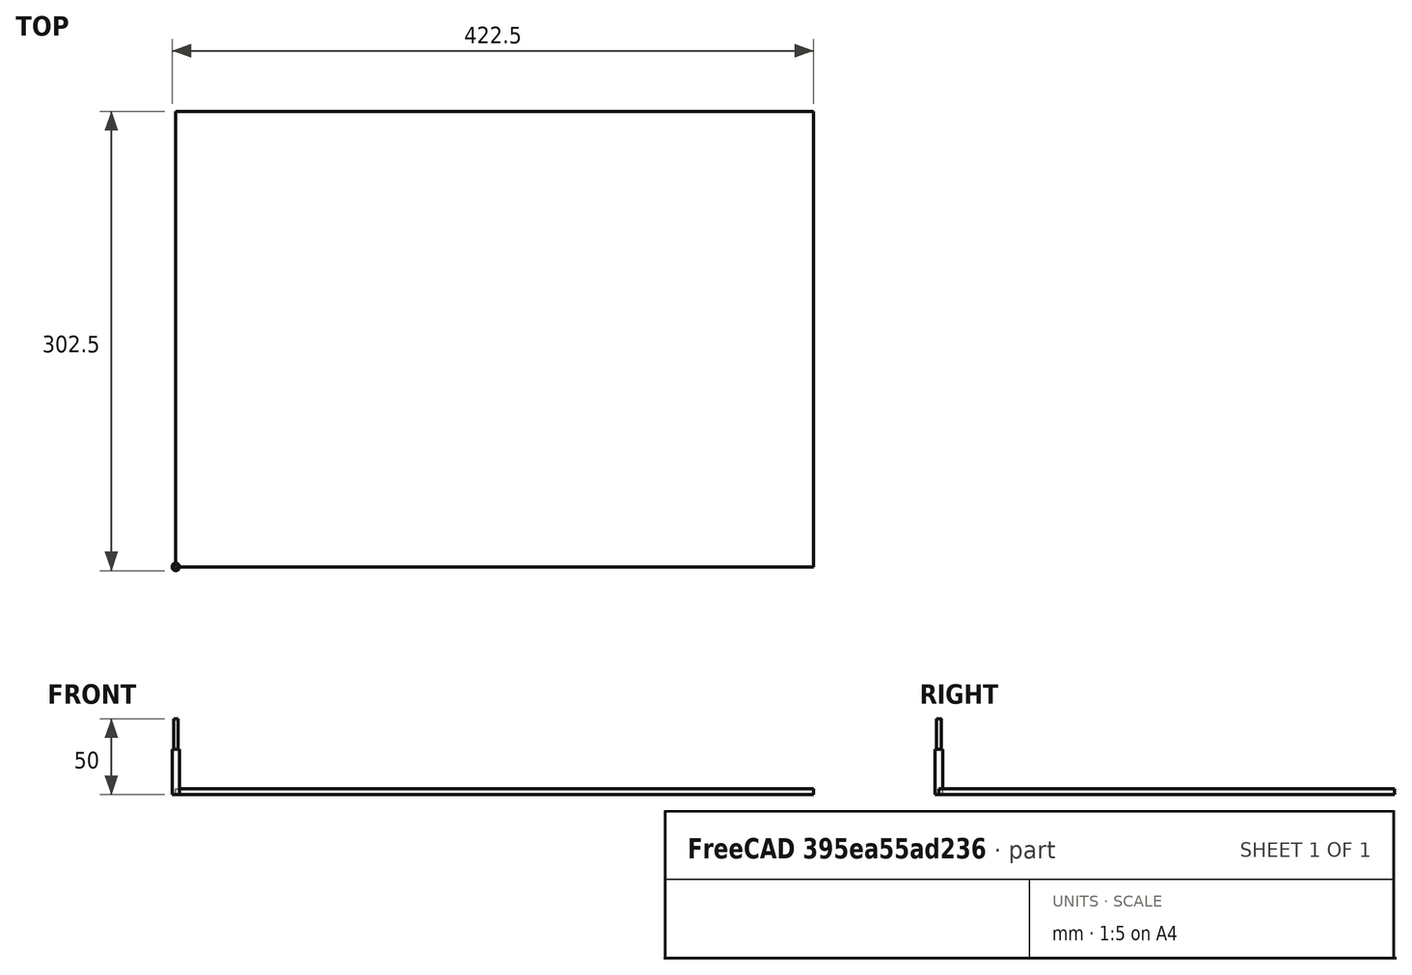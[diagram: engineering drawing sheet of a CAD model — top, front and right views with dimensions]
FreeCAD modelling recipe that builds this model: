
FCSTD DOCUMENT  (FreeCAD 1.0R39109 (Git))
Label: HousingAtari_T02
License: All rights reserved
LicenseURL: https://en.wikipedia.org/wiki/All_rights_reserved
objects: Sketcher::SketchObject×6, Part::Part2DObjectPython×5, Path::FeaturePython×3, App::DocumentObjectGroup×3, Part::FeaturePython×2, PartDesign::Body×1, App::FeaturePython×1, Mesh::FeaturePython×1
note: 20 computed .brp shape members not serialized (recipe doc carries the construction recipe); baked Part::Feature solids carry a one-line shape summary decoded from their .brp

FEATURE [Sketcher::SketchObject] Sketch  label="A3"
  ArcFitTolerance = 0
  FullyConstrained = false
  MakeInternals = false
  MapMode = 5
  sketch-geometry (7):
    g0: LineSegment StartX=0 StartY=420 StartZ=0 EndX=0 EndY=0 EndZ=0
    g1: LineSegment StartX=0 StartY=420 StartZ=0 EndX=148.5 EndY=420 EndZ=0
    g2: LineSegment StartX=148.5 StartY=420 StartZ=0 EndX=148.5 EndY=0 EndZ=0
    g3: LineSegment StartX=148.5 StartY=420 StartZ=0 EndX=297 EndY=420 EndZ=0
    g4: LineSegment StartX=297 StartY=420 StartZ=0 EndX=297 EndY=210 EndZ=0
    g5: LineSegment StartX=297 StartY=210 StartZ=0 EndX=297 EndY=0 EndZ=0
    g6: LineSegment StartX=297 StartY=210 StartZ=0 EndX=0 EndY=210 EndZ=0
  constraints (21):
    c: Vertical(g0)
    c: DistanceY(g0,g0) = 420
    c: Coincident(g1,g0)
    c: Horizontal(g1)
    c: Coincident(g2,g1)
    c: Coincident(g3,g1)
    c: Horizontal(g3)
    c: Equal(g1,g3)
    c: Vertical(g2)
    c: DistanceX(g0,g3) = 297
    c: Coincident(g4,g3)
    c: Vertical(g4)
    c: Coincident(g5,g4)
    c: PointOnObject(g5,g-1)
    c: Vertical(g5)
    c: Equal(g5,g4)
    c: PointOnObject(g0,g-1)
    c: PointOnObject(g0,g-2)
    c: Coincident(g6,g4)
    c: PointOnObject(g6,g0)
    c: Horizontal(g6)
FEATURE [Sketcher::SketchObject] Sketch001  label="BOX-OUTLINE"
  ArcFitTolerance = 0
  ExternalGeometry = -> [Sketch]
  FullyConstrained = false
  MakeInternals = false
  MapMode = 5
  sketch-geometry (60):
    g0: LineSegment StartX=83.5 StartY=362.836 StartZ=0 EndX=83.5 EndY=292.836 EndZ=0
    g1: LineSegment StartX=83.5 StartY=292.836 StartZ=0 EndX=83.5 EndY=222.836 EndZ=0
    g2: LineSegment StartX=83.5 StartY=222.836 StartZ=0 EndX=148.5 EndY=222.836 EndZ=0
    g3: LineSegment StartX=148.5 StartY=222.836 StartZ=0 EndX=213.5 EndY=222.836 EndZ=0
    g4: LineSegment StartX=213.5 StartY=222.836 StartZ=0 EndX=213.5 EndY=292.836 EndZ=0
    g5: LineSegment StartX=213.5 StartY=292.836 StartZ=0 EndX=213.5 EndY=362.836 EndZ=0
    g6: LineSegment StartX=213.5 StartY=362.836 StartZ=0 EndX=148.5 EndY=362.836 EndZ=0
    g7: LineSegment StartX=148.5 StartY=362.836 StartZ=0 EndX=83.5 EndY=362.836 EndZ=0
    g8: LineSegment StartX=83.5 StartY=222.836 StartZ=0 EndX=83.5 EndY=218.836 EndZ=0
    g9: LineSegment StartX=83.5 StartY=218.836 StartZ=0 EndX=213.5 EndY=218.836 EndZ=0
    g10: LineSegment StartX=213.5 StartY=218.836 StartZ=0 EndX=213.5 EndY=222.836 EndZ=0
    g11: LineSegment StartX=213.5 StartY=222.836 StartZ=0 EndX=217.5 EndY=222.836 EndZ=0
    g12: LineSegment StartX=217.5 StartY=222.836 StartZ=0 EndX=217.5 EndY=362.836 EndZ=0
    g13: LineSegment StartX=217.5 StartY=362.836 StartZ=0 EndX=213.5 EndY=362.836 EndZ=0
    g14: LineSegment StartX=213.5 StartY=362.836 StartZ=0 EndX=213.5 EndY=366.836 EndZ=0
    g15: LineSegment StartX=213.5 StartY=366.836 StartZ=0 EndX=83.5 EndY=366.836 EndZ=0
    g16: LineSegment StartX=83.5 StartY=366.836 StartZ=0 EndX=83.5 EndY=362.836 EndZ=0
    g17: LineSegment StartX=83.5 StartY=222.836 StartZ=0 EndX=79.5 EndY=222.836 EndZ=0
    g18: LineSegment StartX=79.5 StartY=222.836 StartZ=0 EndX=79.5 EndY=362.836 EndZ=0
    g19: LineSegment StartX=79.5 StartY=362.836 StartZ=0 EndX=83.5 EndY=362.836 EndZ=0
    g20: LineSegment StartX=83.5 StartY=218.836 StartZ=0 EndX=83.5 EndY=188.836 EndZ=0
    g21: LineSegment StartX=83.5 StartY=188.836 StartZ=0 EndX=213.5 EndY=188.836 EndZ=0
    g22: LineSegment StartX=213.5 StartY=188.836 StartZ=0 EndX=213.5 EndY=218.836 EndZ=0
    g23: LineSegment StartX=217.5 StartY=222.836 StartZ=0 EndX=243.5 EndY=222.836 EndZ=0
    g24: LineSegment StartX=243.5 StartY=222.836 StartZ=0 EndX=243.5 EndY=362.836 EndZ=0
    g25: LineSegment StartX=243.5 StartY=362.836 StartZ=0 EndX=217.5 EndY=362.836 EndZ=0
    g26: LineSegment StartX=213.5 StartY=366.836 StartZ=0 EndX=213.5 EndY=396.836 EndZ=0
    g27: LineSegment StartX=213.5 StartY=396.836 StartZ=0 EndX=83.5 EndY=396.836 EndZ=0
    g28: LineSegment StartX=83.5 StartY=396.836 StartZ=0 EndX=83.5 EndY=366.836 EndZ=0
    g29: LineSegment StartX=79.5 StartY=362.836 StartZ=0 EndX=53.5 EndY=362.836 EndZ=0
    g30: LineSegment StartX=53.5 StartY=362.836 StartZ=0 EndX=53.5 EndY=222.836 EndZ=0
    g31: LineSegment StartX=53.5 StartY=222.836 StartZ=0 EndX=79.5 EndY=222.836 EndZ=0
    g32: LineSegment StartX=213.5 StartY=188.836 StartZ=0 EndX=217.5 EndY=188.836 EndZ=0
    g33: LineSegment StartX=217.5 StartY=188.836 StartZ=0 EndX=217.5 EndY=222.836 EndZ=0
    g34: LineSegment StartX=213.5 StartY=218.836 StartZ=0 EndX=243.5 EndY=218.836 EndZ=0
    g35: LineSegment StartX=243.5 StartY=218.836 StartZ=0 EndX=243.5 EndY=222.836 EndZ=0
    g36: LineSegment StartX=213.5 StartY=366.836 StartZ=0 EndX=243.5 EndY=366.836 EndZ=0
    g37: LineSegment StartX=243.5 StartY=366.836 StartZ=0 EndX=243.5 EndY=362.836 EndZ=0
    g38: LineSegment StartX=217.5 StartY=362.836 StartZ=0 EndX=217.5 EndY=396.836 EndZ=0
    g39: LineSegment StartX=217.5 StartY=396.836 StartZ=0 EndX=213.5 EndY=396.836 EndZ=0
    g40: LineSegment StartX=83.5 StartY=396.836 StartZ=0 EndX=79.5 EndY=396.836 EndZ=0
    g41: LineSegment StartX=79.5 StartY=396.836 StartZ=0 EndX=79.5 EndY=362.836 EndZ=0
    g42: LineSegment StartX=53.5 StartY=362.836 StartZ=0 EndX=53.5 EndY=366.836 EndZ=0
    g43: LineSegment StartX=53.5 StartY=366.836 StartZ=0 EndX=83.5 EndY=366.836 EndZ=0
    g44: LineSegment StartX=53.5 StartY=222.836 StartZ=0 EndX=53.5 EndY=218.836 EndZ=0
    g45: LineSegment StartX=53.5 StartY=218.836 StartZ=0 EndX=83.5 EndY=218.836 EndZ=0
    g46: LineSegment StartX=79.5 StartY=222.836 StartZ=0 EndX=79.5 EndY=188.836 EndZ=0
    g47: LineSegment StartX=79.5 StartY=188.836 StartZ=0 EndX=83.5 EndY=188.836 EndZ=0
    g48: LineSegment StartX=83.5 StartY=188.836 StartZ=0 EndX=83.5 EndY=44.8363 EndZ=0
    g49: LineSegment StartX=83.5 StartY=44.8363 StartZ=0 EndX=213.5 EndY=44.8363 EndZ=0
    g50: LineSegment StartX=213.5 StartY=44.8363 StartZ=0 EndX=213.5 EndY=188.836 EndZ=0
    g51: LineSegment StartX=79.5 StartY=188.836 StartZ=0 EndX=79.5 EndY=48.8363 EndZ=0
    g52: LineSegment StartX=79.5 StartY=48.8363 StartZ=0 EndX=217.5 EndY=48.8363 EndZ=0
    g53: LineSegment StartX=217.5 StartY=48.8363 StartZ=0 EndX=217.5 EndY=188.836 EndZ=0
    g54: LineSegment StartX=79.5 StartY=192.836 StartZ=0 EndX=217.5 EndY=192.836 EndZ=0
    g55: LineSegment StartX=79.5 StartY=48.8363 StartZ=0 EndX=79.5 EndY=44.8363 EndZ=0
    g56: LineSegment StartX=217.5 StartY=48.8363 StartZ=0 EndX=217.5 EndY=44.8363 EndZ=0
    g57: LineSegment StartX=79.5 StartY=392.836 StartZ=0 EndX=217.5 EndY=392.836 EndZ=0
    g58: LineSegment StartX=247.5 StartY=366.836 StartZ=0 EndX=247.5 EndY=218.836 EndZ=0
    g59: LineSegment StartX=49.5 StartY=366.836 StartZ=0 EndX=49.5 EndY=218.836 EndZ=0
  constraints (166):
    c: Vertical(g0)
    c: Coincident(g1,g0)
    c: Vertical(g1)
    c: Coincident(g2,g1)
    c: Horizontal(g2)
    c: Coincident(g3,g2)
    c: Horizontal(g3)
    c: Coincident(g4,g3)
    c: Vertical(g4)
    c: Coincident(g5,g4)
    c: Vertical(g5)
    c: Horizontal(g6)
    c: Coincident(g7,g6)
    c: Coincident(g7,g0)
    c: Horizontal(g7)
    c: Vertical(g2,g6)
    c: Horizontal(g0,g4)
    c: Equal(g4,g5)
    c: Equal(g7,g6)
    c: Coincident(g5,g6)
    c: DistanceY(g1,g0) = 140
    c: DistanceX(g0,g5) = 130
    c: Coincident(g8,g1)
    c: Vertical(g8)
    c: Coincident(g9,g8)
    c: Horizontal(g9)
    c: Coincident(g10,g9)
    c: Coincident(g10,g3)
    c: Vertical(g10)
    c: Coincident(g11,g3)
    c: Horizontal(g11)
    c: Coincident(g12,g11)
    c: Vertical(g12)
    c: Coincident(g13,g12)
    c: Coincident(g13,g5)
    c: Horizontal(g13)
    c: Equal(g10,g11)
    c: DistanceY(g10,g10) = 4
    c: Coincident(g14,g5)
    c: Vertical(g14)
    c: Coincident(g15,g14)
    c: Horizontal(g15)
    c: Coincident(g16,g15)
    c: Coincident(g16,g0)
    c: Vertical(g16)
    c: Equal(g13,g14)
    c: Coincident(g17,g1)
    c: Horizontal(g17)
    c: Coincident(g18,g17)
    c: Vertical(g18)
    c: Coincident(g19,g18)
    c: Coincident(g19,g0)
    c: Horizontal(g19)
    c: Equal(g16,g19)
    c: Coincident(g20,g8)
    c: Vertical(g20)
    c: Coincident(g21,g20)
    c: Horizontal(g21)
    c: Coincident(g22,g21)
    c: Coincident(g22,g9)
    c: Coincident(g23,g11)
    c: Horizontal(g23)
    c: Coincident(g24,g23)
    c: Vertical(g24)
    c: Coincident(g25,g24)
    c: Coincident(g25,g12)
    c: Horizontal(g25)
    c: Coincident(g26,g14)
    c: Vertical(g26)
    c: Coincident(g27,g26)
    c: Horizontal(g27)
    c: Coincident(g28,g27)
    c: Coincident(g28,g15)
    c: Coincident(g29,g18)
    c: Horizontal(g29)
    c: Coincident(g30,g29)
    c: Vertical(g30)
    c: Coincident(g31,g30)
    c: Coincident(g31,g17)
    c: Horizontal(g31)
    c: Vertical(g22)
    c: Coincident(g32,g21)
    c: Horizontal(g32)
    c: Coincident(g33,g32)
    c: Coincident(g33,g11)
    c: Vertical(g33)
    c: Coincident(g34,g9)
    c: Horizontal(g34)
    c: Coincident(g35,g34)
    c: Coincident(g35,g23)
    c: Coincident(g36,g14)
    c: Horizontal(g36)
    c: Coincident(g37,g36)
    c: Coincident(g37,g24)
    c: Coincident(g38,g12)
    c: Vertical(g38)
    c: Coincident(g39,g38)
    c: Coincident(g39,g26)
    c: Horizontal(g39)
    c: Coincident(g40,g27)
    c: Horizontal(g40)
    c: Coincident(g41,g40)
    c: Coincident(g41,g18)
    c: Coincident(g42,g29)
    c: Vertical(g42)
    c: Coincident(g43,g42)
    c: Coincident(g43,g15)
    c: Coincident(g44,g30)
    c: Vertical(g44)
    c: Coincident(g45,g44)
    c: Coincident(g45,g8)
    c: Horizontal(g45)
    c: Coincident(g46,g17)
    c: Coincident(g47,g46)
    c: Coincident(g47,g20)
    c: Vertical(g37)
    c: Vertical(g46)
    c: Vertical(g35)
    c: Horizontal(g43)
    c: Horizontal(g47)
    c: DistanceY(g15,g27) = 30
    c: Vertical(g41)
    c: Vertical(g28)
    c: DistanceY(g22,g22) = 30
    c: Distance(g43,g43) = 30
    c: DistanceX(g34,g34) = 30
    c: Coincident(g48,g20)
    c: Vertical(g48)
    c: Coincident(g49,g48)
    c: Horizontal(g49)
    c: Coincident(g50,g49)
    c: Coincident(g50,g21)
    c: Vertical(g50)
    c: Coincident(g51,g46)
    c: Vertical(g51)
    c: Coincident(g52,g51)
    c: Horizontal(g52)
    c: Coincident(g53,g52)
    c: Coincident(g53,g32)
    c: Vertical(g53)
    c: PointOnObject(g54,g46)
    c: PointOnObject(g54,g33)
    c: Horizontal(g54)
    c: DistanceY(g46,g54) = 4
    c: Coincident(g55,g51)
    c: PointOnObject(g55,g49)
    c: Vertical(g55)
    c: DistanceY(g55,g55) = 4
    c: DistanceY(g51,g51) = 140
    c: DistanceY(g34,g36) = 148
    c: Coincident(g56,g52)
    c: PointOnObject(g56,g49)
    c: Vertical(g56)
    c: DistanceY(g56,g54) = 148
    c: PointOnObject(g57,g41)
    c: PointOnObject(g57,g38)
    c: Horizontal(g57)
    c: DistanceY(g57,g38) = 4
    c: PointOnObject(g6,g-3)
    c: PointOnObject(g58,g36)
    c: PointOnObject(g58,g34)
    c: Vertical(g58)
    c: PointOnObject(g59,g43)
    c: PointOnObject(g59,g45)
    c: Vertical(g59)
    c: DistanceX(g42,g59) = -4
FEATURE [PartDesign::Body] Body
  AllowCompound = false
  Group = -> [Sketch,Sketch001]
  Origin = -> Origin
FEATURE [Sketcher::SketchObject] Sketch002  label="CUT-BOX-BASE"
  ArcFitTolerance = 0
  ExternalGeometry = -> [Sketch001,Sketch]
  FullyConstrained = true
  MakeInternals = false
  MapMode = 5
  sketch-geometry (44):
    g0: LineSegment StartX=107.1 StartY=366.836 StartZ=0 EndX=79.5 EndY=366.836 EndZ=0
    g1: LineSegment StartX=189.9 StartY=366.836 StartZ=0 EndX=217.5 EndY=366.836 EndZ=0
    g2: LineSegment StartX=134.7 StartY=366.836 StartZ=0 EndX=162.3 EndY=366.836 EndZ=0
    g3: LineSegment StartX=162.3 StartY=362.836 StartZ=0 EndX=189.9 EndY=362.836 EndZ=0
    g4: LineSegment StartX=107.1 StartY=362.836 StartZ=0 EndX=134.7 EndY=362.836 EndZ=0
    g5: LineSegment StartX=107.1 StartY=366.836 StartZ=0 EndX=107.1 EndY=362.836 EndZ=0
    g6: LineSegment StartX=134.7 StartY=366.836 StartZ=0 EndX=134.7 EndY=362.836 EndZ=0
    g7: LineSegment StartX=162.3 StartY=366.836 StartZ=0 EndX=162.3 EndY=362.836 EndZ=0
    g8: LineSegment StartX=189.9 StartY=362.836 StartZ=0 EndX=189.9 EndY=366.836 EndZ=0
    g9: LineSegment [constr] StartX=107.1 StartY=362.836 StartZ=0 EndX=107.1 EndY=222.836 EndZ=0
    g10: LineSegment [constr] StartX=134.7 StartY=362.836 StartZ=0 EndX=134.7 EndY=222.836 EndZ=0
    g11: LineSegment [constr] StartX=162.3 StartY=362.836 StartZ=0 EndX=162.3 EndY=222.836 EndZ=0
    g12: LineSegment [constr] StartX=189.9 StartY=362.836 StartZ=0 EndX=189.9 EndY=222.836 EndZ=0
    g13: LineSegment StartX=79.5 StartY=218.836 StartZ=0 EndX=107.1 EndY=218.836 EndZ=0
    g14: LineSegment StartX=107.1 StartY=218.836 StartZ=0 EndX=107.1 EndY=222.836 EndZ=0
    g15: LineSegment StartX=107.1 StartY=222.836 StartZ=0 EndX=134.7 EndY=222.836 EndZ=0
    g16: LineSegment StartX=134.7 StartY=222.836 StartZ=0 EndX=134.7 EndY=218.836 EndZ=0
    g17: LineSegment StartX=134.7 StartY=218.836 StartZ=0 EndX=162.3 EndY=218.836 EndZ=0
    g18: LineSegment StartX=162.3 StartY=218.836 StartZ=0 EndX=162.3 EndY=222.836 EndZ=0
    g19: LineSegment StartX=162.3 StartY=222.836 StartZ=0 EndX=189.9 EndY=222.836 EndZ=0
    g20: LineSegment StartX=189.9 StartY=222.836 StartZ=0 EndX=189.9 EndY=218.836 EndZ=0
    g21: LineSegment StartX=189.9 StartY=218.836 StartZ=0 EndX=217.5 EndY=218.836 EndZ=0
    g22: LineSegment StartX=79.5 StartY=366.836 StartZ=0 EndX=79.5 EndY=336.163 EndZ=0
    g23: LineSegment StartX=79.5 StartY=305.49 StartZ=0 EndX=79.5 EndY=274.818 EndZ=0
    g24: LineSegment StartX=79.5 StartY=218.836 StartZ=0 EndX=79.5 EndY=244.145 EndZ=0
    g25: LineSegment StartX=79.5 StartY=336.163 StartZ=0 EndX=83.5 EndY=336.163 EndZ=0
    g26: LineSegment StartX=79.5 StartY=305.49 StartZ=0 EndX=83.5 EndY=305.49 EndZ=0
    g27: LineSegment StartX=79.5 StartY=274.818 StartZ=0 EndX=83.5 EndY=274.818 EndZ=0
    g28: LineSegment StartX=79.5 StartY=244.145 StartZ=0 EndX=83.5 EndY=244.145 EndZ=0
    g29: LineSegment StartX=83.5 StartY=305.49 StartZ=0 EndX=83.5 EndY=336.163 EndZ=0
    g30: LineSegment StartX=83.5 StartY=244.145 StartZ=0 EndX=83.5 EndY=274.818 EndZ=0
    g31: LineSegment [constr] StartX=83.5 StartY=336.163 StartZ=0 EndX=213.5 EndY=336.163 EndZ=0
    g32: LineSegment [constr] StartX=83.5 StartY=305.49 StartZ=0 EndX=213.5 EndY=305.49 EndZ=0
    g33: LineSegment [constr] StartX=83.5 StartY=274.818 StartZ=0 EndX=213.5 EndY=274.818 EndZ=0
    g34: LineSegment [constr] StartX=83.5 StartY=244.145 StartZ=0 EndX=213.5 EndY=244.145 EndZ=0
    g35: LineSegment StartX=217.5 StartY=366.836 StartZ=0 EndX=217.5 EndY=336.163 EndZ=0
    g36: LineSegment StartX=213.5 StartY=336.163 StartZ=0 EndX=217.5 EndY=336.163 EndZ=0
    g37: LineSegment StartX=213.5 StartY=305.49 StartZ=0 EndX=213.5 EndY=336.163 EndZ=0
    g38: LineSegment StartX=213.5 StartY=305.49 StartZ=0 EndX=217.5 EndY=305.49 EndZ=0
    g39: LineSegment StartX=213.5 StartY=274.818 StartZ=0 EndX=213.5 EndY=244.145 EndZ=0
    g40: LineSegment StartX=213.5 StartY=244.145 StartZ=0 EndX=217.5 EndY=244.145 EndZ=0
    g41: LineSegment StartX=217.5 StartY=244.145 StartZ=0 EndX=217.5 EndY=218.836 EndZ=0
    g42: LineSegment StartX=213.5 StartY=274.818 StartZ=0 EndX=217.5 EndY=274.818 EndZ=0
    g43: LineSegment StartX=217.5 StartY=274.818 StartZ=0 EndX=217.5 EndY=305.49 EndZ=0
  constraints (126):
    c: PointOnObject(g0,g-5)
    c: PointOnObject(g0,g-9)
    c: Horizontal(g0)
    c: PointOnObject(g1,g-5)
    c: PointOnObject(g1,g-10)
    c: Horizontal(g1)
    c: PointOnObject(g2,g-5)
    c: PointOnObject(g2,g-5)
    c: PointOnObject(g3,g-4)
    c: PointOnObject(g3,g-4)
    c: PointOnObject(g4,g-3)
    c: PointOnObject(g4,g-3)
    c: Coincident(g5,g0)
    c: Coincident(g5,g4)
    c: Coincident(g6,g2)
    c: Coincident(g6,g4)
    c: Coincident(g7,g2)
    c: Coincident(g7,g3)
    c: Coincident(g8,g3)
    c: Coincident(g8,g1)
    c: Vertical(g5)
    c: Vertical(g6)
    c: Vertical(g7)
    c: Vertical(g8)
    c: Equal(g0,g1)
    c: Equal(g4,g2)
    c: Equal(g3,g2)
    c: Equal(g0,g2)
    c: Coincident(g9,g4)
    c: PointOnObject(g9,g-6)
    c: Vertical(g9)
    c: Coincident(g10,g4)
    c: PointOnObject(g10,g-6)
    c: Vertical(g10)
    c: Coincident(g11,g3)
    c: PointOnObject(g11,g-8)
    c: Vertical(g11)
    c: Coincident(g12,g3)
    c: PointOnObject(g12,g-8)
    c: Vertical(g12)
    c: PointOnObject(g13,g-12)
    c: PointOnObject(g13,g-7)
    c: Horizontal(g13)
    c: Coincident(g14,g13)
    c: Coincident(g14,g9)
    c: Coincident(g15,g9)
    c: Coincident(g15,g10)
    c: Coincident(g16,g10)
    c: PointOnObject(g16,g-7)
    c: Coincident(g17,g16)
    c: PointOnObject(g17,g-7)
    c: Coincident(g18,g17)
    c: Coincident(g18,g11)
    c: Coincident(g19,g11)
    c: Coincident(g19,g12)
    c: Coincident(g20,g12)
    c: PointOnObject(g20,g-7)
    c: Vertical(g20)
    c: Coincident(g21,g20)
    c: PointOnObject(g21,g-11)
    c: Horizontal(g21)
    c: Vertical(g14)
    c: Vertical(g16)
    c: Vertical(g18)
    c: DistanceY(g21,g1) = 148
    c: DistanceX(g0,g1) = 138
    c: Coincident(g22,g0)
    c: PointOnObject(g22,g-14)
    c: PointOnObject(g23,g-14)
    c: PointOnObject(g23,g-14)
    c: Coincident(g24,g13)
    c: PointOnObject(g24,g-14)
    c: Coincident(g25,g22)
    c: PointOnObject(g25,g-16)
    c: Horizontal(g25)
    c: Coincident(g26,g23)
    c: PointOnObject(g26,g-16)
    c: Horizontal(g26)
    c: Coincident(g27,g23)
    c: PointOnObject(g27,g-17)
    c: Coincident(g28,g24)
    c: PointOnObject(g28,g-17)
    c: Horizontal(g28)
    c: Horizontal(g27)
    c: Equal(g22,g23)
    c: Coincident(g29,g26)
    c: Coincident(g29,g25)
    c: Coincident(g30,g28)
    c: Coincident(g30,g27)
    c: Equal(g30,g23)
    c: Equal(g29,g30)
    c: Equal(g29,g22)
    c: Coincident(g31,g25)
    c: PointOnObject(g31,g-18)
    c: Horizontal(g31)
    c: Coincident(g32,g26)
    c: PointOnObject(g32,g-18)
    c: Horizontal(g32)
    c: Coincident(g33,g27)
    c: PointOnObject(g33,g-19)
    c: Horizontal(g33)
    c: Coincident(g34,g28)
    c: PointOnObject(g34,g-19)
    c: Horizontal(g34)
    c: Coincident(g35,g1)
    c: PointOnObject(g35,g-15)
    c: Coincident(g36,g31)
    c: Coincident(g36,g35)
    c: Coincident(g37,g32)
    c: Coincident(g37,g31)
    c: Coincident(g38,g32)
    c: PointOnObject(g38,g-15)
    c: Coincident(g39,g33)
    c: Coincident(g39,g34)
    c: Coincident(g40,g34)
    c: PointOnObject(g40,g-15)
    c: Coincident(g41,g40)
    c: Coincident(g41,g21)
    c: Horizontal(g36)
    c: Horizontal(g38)
    c: Horizontal(g40)
    c: Coincident(g42,g33)
    c: PointOnObject(g42,g-15)
    c: Horizontal(g42)
    c: Coincident(g43,g42)
    c: Coincident(g43,g38)
FEATURE [Sketcher::SketchObject] Sketch003  label="CUT-Functional"
  ArcFitTolerance = 0
  ExternalGeometry = -> [Sketch]
  FullyConstrained = false
  MakeInternals = false
  MapMode = 5
  sketch-geometry (23):
    g0: LineSegment [constr] StartX=118.5 StartY=350.114 StartZ=0 EndX=148.5 EndY=350.114 EndZ=0
    g1: LineSegment [constr] StartX=148.5 StartY=350.114 StartZ=0 EndX=178.5 EndY=350.114 EndZ=0
    g2: Circle CenterX=118.5 CenterY=350.114 CenterZ=0 NormalX=0 NormalY=0 NormalZ=1 AngleXU=0 Radius=8
    g3: Circle CenterX=148.5 CenterY=350.114 CenterZ=0 NormalX=0 NormalY=0 NormalZ=1 AngleXU=0 Radius=8
    g4: Circle CenterX=178.5 CenterY=350.114 CenterZ=0 NormalX=0 NormalY=0 NormalZ=1 AngleXU=0 Radius=8
    g5: Circle CenterX=163.5 CenterY=331.863 CenterZ=0 NormalX=0 NormalY=0 NormalZ=1 AngleXU=0 Radius=8
    g6: Circle CenterX=133.5 CenterY=331.863 CenterZ=0 NormalX=0 NormalY=0 NormalZ=1 AngleXU=0 Radius=8
    g7: LineSegment [constr] StartX=133.5 StartY=331.863 StartZ=0 EndX=163.5 EndY=331.863 EndZ=0
    g8: LineSegment [constr] StartX=133.5 StartY=331.863 StartZ=0 EndX=118.5 EndY=350.114 EndZ=0
    g9: LineSegment [constr] StartX=163.5 StartY=331.863 StartZ=0 EndX=178.5 EndY=350.114 EndZ=0
    g10: LineSegment StartX=136 StartY=316.42 StartZ=0 EndX=136 EndY=306.42 EndZ=0
    g11: LineSegment StartX=136 StartY=306.42 StartZ=0 EndX=161 EndY=306.42 EndZ=0
    g12: LineSegment StartX=161 StartY=306.42 StartZ=0 EndX=161 EndY=316.42 EndZ=0
    g13: LineSegment StartX=136 StartY=316.42 StartZ=0 EndX=148.5 EndY=316.42 EndZ=0
    g14: LineSegment StartX=161 StartY=316.42 StartZ=0 EndX=148.5 EndY=316.42 EndZ=0
    g15: ArcOfCircle CenterX=230.249 CenterY=259.609 CenterZ=0 NormalX=0 NormalY=0 NormalZ=1 AngleXU=0 Radius=5 StartAngle=-1.05604e-11 EndAngle=3.14159
    g16: ArcOfCircle CenterX=230.249 CenterY=239.609 CenterZ=0 NormalX=0 NormalY=0 NormalZ=1 AngleXU=0 Radius=5 StartAngle=3.14159 EndAngle=6.28319
    g17: LineSegment StartX=235.249 StartY=259.609 StartZ=0 EndX=235.249 EndY=239.609 EndZ=0
    g18: LineSegment StartX=225.249 StartY=259.609 StartZ=0 EndX=225.249 EndY=239.609 EndZ=0
    g19: LineSegment [constr] StartX=65.9263 StartY=259.117 StartZ=0 EndX=65.9263 EndY=245.113 EndZ=0
    g20: LineSegment [constr] StartX=65.9263 StartY=245.113 StartZ=0 EndX=65.9263 EndY=234.254 EndZ=0
    g21: Circle CenterX=65.9263 CenterY=234.254 CenterZ=0 NormalX=0 NormalY=0 NormalZ=1 AngleXU=0 Radius=2
    g22: Circle CenterX=65.9263 CenterY=259.117 CenterZ=0 NormalX=0 NormalY=0 NormalZ=1 AngleXU=0 Radius=2
  constraints (52):
    c: Horizontal(g0)
    c: Coincident(g1,g0)
    c: Horizontal(g1)
    c: Equal(g1,g0)
    c: Coincident(g2,g0)
    c: Coincident(g3,g0)
    c: Coincident(g4,g1)
    c: Equal(g4,g3)
    c: Equal(g3,g2)
    c: Diameter(g4) = 16
    c: DistanceX(g1,g1) = 30
    c: Coincident(g7,g6)
    c: Coincident(g7,g5)
    c: Equal(g1,g7)
    c: Horizontal(g7)
    c: Coincident(g8,g6)
    c: Coincident(g8,g0)
    c: Coincident(g9,g5)
    c: Coincident(g9,g1)
    c: Equal(g9,g8)
    c: Equal(g4,g5)
    c: Equal(g5,g6)
    c: Coincident(g10,g11)
    c: Coincident(g11,g12)
    c: Vertical(g10)
    c: Vertical(g12)
    c: Horizontal(g11)
    c: Coincident(g13,g10)
    c: PointOnObject(g13,g-3)
    c: Horizontal(g13)
    c: Coincident(g14,g12)
    c: Coincident(g14,g13)
    c: Horizontal(g14)
    c: Equal(g14,g13)
    c: DistanceX(g11,g11) = 25
    c: DistanceY(g12,g12) = 10
    c: PointOnObject(g0,g-3)
    c: Tangent(g15,g17) = 1.5708
    c: Tangent(g15,g18) = -1.5708
    c: Tangent(g16,g17) = 1.5708
    c: Tangent(g16,g18) = -1.5708
    c: Equal(g15,g16)
    c: Vertical(g18)
    c: DistanceX(g15,g15) = 10
    c: DistanceY(g17,g17) = 20
    c: Vertical(g19)
    c: Coincident(g20,g19)
    c: Vertical(g20)
    c: Coincident(g21,g20)
    c: Coincident(g22,g19)
    c: Equal(g22,g21)
    c: Diameter(g22) = 4
FEATURE [App::FeaturePython] SetupSheet  # Path/CAM operation (typed FeaturePython)
  ClearanceHeightExpression = OpStockZMax+SetupSheet.ClearanceHeightOffset
  ClearanceHeightOffset = 5
  CoolantMode = 0
  CoolantModes = None | Flood | Mist
  FinalDepthExpression = OpFinalDepth
  HorizRapid = 0
  SafeHeightExpression = OpStockZMax+SetupSheet.SafeHeightOffset
  SafeHeightOffset = 3
  StartDepthExpression = OpStartDepth
  StepDownExpression = OpToolDiameter
  VertRapid = 0
FEATURE [Part::Part2DObjectPython] Clone2D  label="Model-CUT-BOX"  # Draft 2D object (typed FeaturePython)
  Fuse = false
  Objects = -> [Sketch002]
  PathResource = Model
  Scale = (1,1,1)
FEATURE [Part::Part2DObjectPython] Clone2D001  label="Model-CUT-Functional"  # Draft 2D object (typed FeaturePython)
  Fuse = false
  Objects = -> [Sketch003]
  PathResource = Model
  Scale = (1,1,1)
FEATURE [Part::FeaturePython] ToolBit  label="Endmill"  # Path/CAM toolbit (typed FeaturePython)
  BitPropertyNames = Chipload | CuttingEdgeHeight | Diameter | Flutes | Length | Material | ShankDiameter | SpindleDirection
  BitShape = <path>
  Chipload = 0
  CuttingEdgeHeight = 30
  Diameter = 5
  Flutes = 0
  Length = 50
  Material = 0
  ShankDiameter = 3
  ShapeName = endmill
  SpindleDirection = 0
FEATURE [Path::FeaturePython] TC__Default_Tool  label="TC: Default Tool"  # Path/CAM operation (typed FeaturePython)
  HorizFeed = 1000
  HorizRapid = 1000
  SpindleDir = 0
  SpindleSpeed = 1000
  Tool = -> ToolBit
  ToolNumber = 1
  VertFeed = 1000
  VertRapid = 1000
  expr: HorizRapid = 1000
  expr: VertRapid = 1000
FEATURE [App::DocumentObjectGroup] Tools
  Group = -> [TC__Default_Tool]
FEATURE [Path::FeaturePython] Engrave  # Path/CAM operation (typed FeaturePython)
  Active = true
  ClearanceHeight = 9
  CoolantMode = 0
  CycleTime = 00:00:04
  FinalDepth = -5
  OpFinalDepth = -5
  OpStartDepth = 0
  OpStockZMax = 4
  OpStockZMin = 0
  OpToolDiameter = 5
  SafeHeight = 7
  StartDepth = 0
  StartVertex = 0
  StepDown = 5
  ToolController = -> TC__Default_Tool
  expr: ClearanceHeight = OpStockZMax + SetupSheet.ClearanceHeightOffset
  expr: FinalDepth = OpFinalDepth
  expr: SafeHeight = OpStockZMax + SetupSheet.SafeHeightOffset
  expr: StartDepth = OpStartDepth
  expr: StepDown = OpToolDiameter
FEATURE [App::DocumentObjectGroup] Operations
  Group = -> [Engrave]
FEATURE [Part::FeaturePython] Stock001  # WARN: FeaturePython — macro-defined, semantics opaque (R4)
  Height = 4
  Length = 420
  StockType = CreateBox
  Width = 300
FEATURE [Mesh::FeaturePython] CutMaterial  # WARN: FeaturePython — macro-defined, semantics opaque (R4)
FEATURE [Sketcher::SketchObject] Sketch004  label="CUT-BOX-WALLS"
  ArcFitTolerance = 0
  ExternalGeometry = -> [Sketch001,Sketch002]
  FullyConstrained = false
  MakeInternals = false
  MapMode = 5
  sketch-geometry (99):
    g0: LineSegment [constr] StartX=107.1 StartY=366.836 StartZ=0 EndX=107.1 EndY=396.836 EndZ=0
    g1: LineSegment [constr] StartX=134.7 StartY=366.836 StartZ=0 EndX=134.7 EndY=396.836 EndZ=0
    g2: LineSegment [constr] StartX=162.3 StartY=366.836 StartZ=0 EndX=162.3 EndY=396.836 EndZ=0
    g3: LineSegment [constr] StartX=189.9 StartY=366.836 StartZ=0 EndX=189.9 EndY=396.836 EndZ=0
    g4: LineSegment StartX=79.5 StartY=366.836 StartZ=0 EndX=79.5 EndY=376.836 EndZ=0
    g5: LineSegment StartX=79.5 StartY=376.836 StartZ=0 EndX=83.5 EndY=376.836 EndZ=0
    g6: LineSegment StartX=83.5 StartY=376.836 StartZ=0 EndX=83.5 EndY=386.836 EndZ=0
    g7: LineSegment StartX=83.5 StartY=386.836 StartZ=0 EndX=79.5 EndY=386.836 EndZ=0
    g8: LineSegment StartX=79.5 StartY=386.836 StartZ=0 EndX=79.5 EndY=396.836 EndZ=0
    g9: LineSegment StartX=79.5 StartY=362.836 StartZ=0 EndX=69.5 EndY=362.836 EndZ=0
    g10: LineSegment StartX=69.5 StartY=362.836 StartZ=0 EndX=69.5 EndY=366.836 EndZ=0
    g11: LineSegment StartX=69.5 StartY=366.836 StartZ=0 EndX=59.5 EndY=366.836 EndZ=0
    g12: LineSegment StartX=59.5 StartY=366.836 StartZ=0 EndX=59.5 EndY=362.815 EndZ=0
    g13: LineSegment StartX=59.5 StartY=362.815 StartZ=0 EndX=49.5 EndY=362.815 EndZ=0
    g14: LineSegment [constr] StartX=83.5 StartY=386.836 StartZ=0 EndX=217.5 EndY=386.836 EndZ=0
    g15: LineSegment [constr] StartX=83.5 StartY=376.836 StartZ=0 EndX=217.5 EndY=376.836 EndZ=0
    g16: LineSegment [constr] StartX=189.9 StartY=366.836 StartZ=0 EndX=189.9 EndY=396.836 EndZ=0
    g17: LineSegment StartX=217.5 StartY=366.836 StartZ=0 EndX=217.5 EndY=376.836 EndZ=0
    g18: LineSegment StartX=217.5 StartY=376.836 StartZ=0 EndX=213.5 EndY=376.836 EndZ=0
    g19: LineSegment StartX=213.5 StartY=376.836 StartZ=0 EndX=213.5 EndY=386.836 EndZ=0
    g20: LineSegment StartX=213.5 StartY=386.836 StartZ=0 EndX=217.5 EndY=386.836 EndZ=0
    g21: LineSegment StartX=217.5 StartY=386.836 StartZ=0 EndX=217.5 EndY=396.836 EndZ=0
    g22: LineSegment StartX=227.5 StartY=366.836 StartZ=0 EndX=237.5 EndY=366.836 EndZ=0
    g23: LineSegment StartX=237.5 StartY=366.836 StartZ=0 EndX=237.5 EndY=362.836 EndZ=0
    g24: LineSegment StartX=237.5 StartY=362.836 StartZ=0 EndX=247.5 EndY=362.836 EndZ=0
    g25: LineSegment StartX=217.5 StartY=362.836 StartZ=0 EndX=227.5 EndY=362.836 EndZ=0
    g26: LineSegment StartX=227.5 StartY=362.836 StartZ=0 EndX=227.5 EndY=366.836 EndZ=0
    g27: LineSegment [constr] StartX=59.5 StartY=362.815 StartZ=0 EndX=59.5 EndY=218.836 EndZ=0
    g28: LineSegment [constr] StartX=69.5 StartY=218.836 StartZ=0 EndX=69.5 EndY=362.836 EndZ=0
    g29: LineSegment [constr] StartX=227.5 StartY=362.836 StartZ=0 EndX=227.5 EndY=218.836 EndZ=0
    g30: LineSegment [constr] StartX=237.5 StartY=362.836 StartZ=0 EndX=237.5 EndY=218.836 EndZ=0
    g31: LineSegment StartX=79.5 StartY=222.836 StartZ=0 EndX=69.5 EndY=222.836 EndZ=0
    g32: LineSegment StartX=69.5 StartY=222.836 StartZ=0 EndX=69.5 EndY=218.836 EndZ=0
    g33: LineSegment StartX=69.5 StartY=218.836 StartZ=0 EndX=59.5 EndY=218.836 EndZ=0
    g34: LineSegment StartX=59.5 StartY=222.836 StartZ=0 EndX=59.5 EndY=218.836 EndZ=0
    g35: LineSegment StartX=59.5 StartY=222.836 StartZ=0 EndX=49.5 EndY=222.836 EndZ=0
    g36: LineSegment StartX=217.5 StartY=222.836 StartZ=0 EndX=227.5 EndY=222.836 EndZ=0
    g37: LineSegment StartX=227.5 StartY=222.836 StartZ=0 EndX=227.5 EndY=218.836 EndZ=0
    g38: LineSegment StartX=227.5 StartY=218.836 StartZ=0 EndX=237.5 EndY=218.836 EndZ=0
    g39: LineSegment StartX=247.5 StartY=222.836 StartZ=0 EndX=237.5 EndY=222.836 EndZ=0
    g40: LineSegment StartX=237.5 StartY=222.836 StartZ=0 EndX=237.5 EndY=218.836 EndZ=0
    g41: LineSegment StartX=79.5 StartY=218.836 StartZ=0 EndX=79.5 EndY=208.836 EndZ=0
    g42: LineSegment StartX=79.5 StartY=208.836 StartZ=0 EndX=83.5 EndY=208.836 EndZ=0
    g43: LineSegment StartX=83.5 StartY=208.836 StartZ=0 EndX=83.5 EndY=198.836 EndZ=0
    g44: LineSegment StartX=83.5 StartY=198.836 StartZ=0 EndX=79.5 EndY=198.836 EndZ=0
    g45: LineSegment StartX=79.5 StartY=198.836 StartZ=0 EndX=79.5 EndY=188.836 EndZ=0
    g46: LineSegment [constr] StartX=83.5 StartY=208.836 StartZ=0 EndX=213.5 EndY=208.836 EndZ=0
    g47: LineSegment [constr] StartX=83.5 StartY=198.836 StartZ=0 EndX=213.5 EndY=198.836 EndZ=0
    g48: LineSegment StartX=217.5 StartY=218.836 StartZ=0 EndX=217.5 EndY=208.836 EndZ=0
    g49: LineSegment StartX=217.5 StartY=208.836 StartZ=0 EndX=213.5 EndY=208.836 EndZ=0
    g50: LineSegment StartX=213.5 StartY=208.836 StartZ=0 EndX=213.5 EndY=198.836 EndZ=0
    g51: LineSegment StartX=213.5 StartY=198.836 StartZ=0 EndX=217.5 EndY=198.836 EndZ=0
    g52: LineSegment StartX=217.5 StartY=198.836 StartZ=0 EndX=217.5 EndY=188.836 EndZ=0
    g53: LineSegment [constr] StartX=49.5 StartY=336.163 StartZ=0 EndX=247.5 EndY=336.163 EndZ=0
    g54: LineSegment [constr] StartX=49.5 StartY=305.49 StartZ=0 EndX=247.5 EndY=305.49 EndZ=0
    g55: LineSegment [constr] StartX=49.5 StartY=274.818 StartZ=0 EndX=247.5 EndY=274.818 EndZ=0
    g56: LineSegment [constr] StartX=49.5 StartY=244.145 StartZ=0 EndX=247.5 EndY=244.145 EndZ=0
    g57: LineSegment [constr] StartX=107.1 StartY=396.836 StartZ=0 EndX=107.1 EndY=392.836 EndZ=0
    g58: LineSegment StartX=79.5 StartY=396.836 StartZ=0 EndX=107.1 EndY=396.836 EndZ=0
    g59: LineSegment StartX=107.1 StartY=392.836 StartZ=0 EndX=107.1 EndY=396.836 EndZ=0
    g60: LineSegment StartX=107.1 StartY=392.836 StartZ=0 EndX=134.7 EndY=392.836 EndZ=0
    g61: LineSegment StartX=134.7 StartY=392.836 StartZ=0 EndX=134.7 EndY=396.836 EndZ=0
    g62: LineSegment StartX=134.7 StartY=396.836 StartZ=0 EndX=162.3 EndY=396.836 EndZ=0
    g63: LineSegment StartX=162.3 StartY=396.836 StartZ=0 EndX=162.3 EndY=392.836 EndZ=0
    g64: LineSegment StartX=162.3 StartY=392.836 StartZ=0 EndX=189.9 EndY=392.836 EndZ=0
    g65: LineSegment StartX=189.9 StartY=392.836 StartZ=0 EndX=189.9 EndY=396.836 EndZ=0
    g66: LineSegment StartX=189.9 StartY=396.836 StartZ=0 EndX=217.5 EndY=396.836 EndZ=0
    g67: LineSegment [constr] StartX=107.1 StartY=362.836 StartZ=0 EndX=107.1 EndY=188.836 EndZ=0
    g68: LineSegment [constr] StartX=134.7 StartY=362.836 StartZ=0 EndX=134.7 EndY=188.836 EndZ=0
    g69: LineSegment [constr] StartX=162.3 StartY=362.836 StartZ=0 EndX=162.3 EndY=188.836 EndZ=0
    g70: LineSegment [constr] StartX=189.9 StartY=362.836 StartZ=0 EndX=189.9 EndY=188.836 EndZ=0
    g71: LineSegment StartX=79.5 StartY=188.836 StartZ=0 EndX=107.1 EndY=188.836 EndZ=0
    g72: LineSegment StartX=134.7 StartY=188.836 StartZ=0 EndX=162.3 EndY=188.836 EndZ=0
    g73: LineSegment StartX=189.9 StartY=188.836 StartZ=0 EndX=217.5 EndY=188.836 EndZ=0
    g74: LineSegment [constr] StartX=107.1 StartY=188.836 StartZ=0 EndX=107.1 EndY=192.836 EndZ=0
    g75: LineSegment StartX=107.1 StartY=188.836 StartZ=0 EndX=107.1 EndY=192.836 EndZ=0
    g76: LineSegment StartX=107.1 StartY=192.836 StartZ=0 EndX=134.7 EndY=192.836 EndZ=0
    g77: LineSegment StartX=134.7 StartY=192.836 StartZ=0 EndX=134.7 EndY=188.836 EndZ=0
    g78: LineSegment StartX=162.3 StartY=188.836 StartZ=0 EndX=162.3 EndY=192.836 EndZ=0
    g79: LineSegment StartX=162.3 StartY=192.836 StartZ=0 EndX=189.9 EndY=192.836 EndZ=0
    g80: LineSegment StartX=189.9 StartY=192.836 StartZ=0 EndX=189.9 EndY=188.836 EndZ=0
    g81: LineSegment StartX=49.5 StartY=222.836 StartZ=0 EndX=49.5 EndY=244.145 EndZ=0
    g82: LineSegment StartX=49.5 StartY=244.145 StartZ=0 EndX=53.5 EndY=244.145 EndZ=0
    g83: LineSegment StartX=53.5 StartY=244.145 StartZ=0 EndX=53.5 EndY=274.818 EndZ=0
    g84: LineSegment StartX=53.5 StartY=274.818 StartZ=0 EndX=49.5 EndY=274.818 EndZ=0
    g85: LineSegment StartX=49.5 StartY=274.818 StartZ=0 EndX=49.5 EndY=305.49 EndZ=0
    g86: LineSegment StartX=49.5 StartY=305.49 StartZ=0 EndX=53.5 EndY=305.49 EndZ=0
    g87: LineSegment StartX=53.5 StartY=305.49 StartZ=0 EndX=53.5 EndY=336.163 EndZ=0
    g88: LineSegment StartX=53.5 StartY=336.163 StartZ=0 EndX=49.5 EndY=336.163 EndZ=0
    g89: LineSegment StartX=49.5 StartY=336.163 StartZ=0 EndX=49.5 EndY=362.815 EndZ=0
    g90: LineSegment StartX=247.5 StartY=222.836 StartZ=0 EndX=247.5 EndY=244.145 EndZ=0
    g91: LineSegment StartX=247.5 StartY=244.145 StartZ=0 EndX=243.5 EndY=244.145 EndZ=0
    g92: LineSegment StartX=243.5 StartY=244.145 StartZ=0 EndX=243.5 EndY=274.818 EndZ=0
    g93: LineSegment StartX=243.5 StartY=274.818 StartZ=0 EndX=247.5 EndY=274.818 EndZ=0
    g94: LineSegment StartX=247.5 StartY=274.818 StartZ=0 EndX=247.5 EndY=305.49 EndZ=0
    g95: LineSegment StartX=247.5 StartY=362.836 StartZ=0 EndX=247.5 EndY=336.163 EndZ=0
    g96: LineSegment StartX=247.5 StartY=336.163 StartZ=0 EndX=243.5 EndY=336.163 EndZ=0
    g97: LineSegment StartX=243.5 StartY=336.163 StartZ=0 EndX=243.5 EndY=305.329 EndZ=0
    g98: LineSegment StartX=243.5 StartY=305.329 StartZ=0 EndX=247.5 EndY=305.49 EndZ=0
  constraints (273):
    c: Coincident(g0,g-18)
    c: PointOnObject(g0,g-22)
    c: Vertical(g0)
    c: Coincident(g1,g-17)
    c: PointOnObject(g1,g-22)
    c: Vertical(g1)
    c: Coincident(g2,g-16)
    c: PointOnObject(g2,g-22)
    c: Vertical(g2)
    c: Coincident(g3,g-15)
    c: PointOnObject(g3,g-22)
    c: Vertical(g3)
    c: PointOnObject(g4,g-27)
    c: PointOnObject(g4,g-27)
    c: Coincident(g5,g4)
    c: PointOnObject(g5,g-31)
    c: Horizontal(g5)
    c: Coincident(g6,g5)
    c: PointOnObject(g6,g-31)
    c: Coincident(g7,g6)
    c: PointOnObject(g7,g-27)
    c: Horizontal(g7)
    c: Coincident(g8,g7)
    c: Coincident(g8,g-27)
    c: Equal(g4,g6)
    c: Equal(g6,g8)
    c: PointOnObject(g4,g-23)
    c: Coincident(g9,g-27)
    c: Horizontal(g9)
    c: Coincident(g10,g9)
    c: PointOnObject(g10,g-23)
    c: Vertical(g10)
    c: Coincident(g11,g10)
    c: PointOnObject(g11,g-23)
    c: Coincident(g12,g11)
    c: Vertical(g12)
    c: Equal(g9,g4)
    c: Equal(g11,g6)
    c: DistanceY(g0,g0) = 30
    c: DistanceX(g-32,g-3) = 30
    c: Coincident(g13,g12)
    c: PointOnObject(g13,g-32)
    c: Horizontal(g13)
    c: Equal(g13,g11)
    c: DistanceY(g-29,g-33) = 30
    c: Coincident(g14,g6)
    c: PointOnObject(g14,g-28)
    c: Horizontal(g14)
    c: Coincident(g15,g5)
    c: PointOnObject(g15,g-28)
    c: Horizontal(g15)
    c: Coincident(g16,g-15)
    c: PointOnObject(g16,g-22)
    c: Vertical(g16)
    c: PointOnObject(g17,g-24)
    c: Coincident(g17,g15)
    c: Vertical(g17)
    c: Coincident(g18,g15)
    c: PointOnObject(g18,g-34)
    c: Horizontal(g18)
    c: Coincident(g19,g18)
    c: PointOnObject(g19,g-34)
    c: Coincident(g20,g19)
    c: Coincident(g20,g14)
    c: Horizontal(g20)
    c: Coincident(g21,g14)
    c: Coincident(g21,g-28)
    c: PointOnObject(g22,g-24)
    c: Coincident(g23,g22)
    c: Vertical(g23)
    c: Coincident(g24,g23)
    c: PointOnObject(g24,g-33)
    c: Horizontal(g24)
    c: PointOnObject(g22,g-24)
    c: PointOnObject(g-20,g24)
    c: Equal(g24,g22)
    c: Equal(g22,g19)
    c: Coincident(g25,g-28)
    c: Horizontal(g25)
    c: Coincident(g26,g25)
    c: Coincident(g26,g22)
    c: Vertical(g26)
    c: Coincident(g27,g12)
    c: PointOnObject(g27,g-26)
    c: Vertical(g27)
    c: PointOnObject(g28,g-26)
    c: Coincident(g28,g9)
    c: Vertical(g28)
    c: Coincident(g29,g25)
    c: PointOnObject(g29,g-25)
    c: Vertical(g29)
    c: Coincident(g30,g23)
    c: PointOnObject(g30,g-25)
    c: Vertical(g30)
    c: Coincident(g31,g-30)
    c: PointOnObject(g31,g28)
    c: Horizontal(g31)
    c: Coincident(g32,g31)
    c: Coincident(g32,g28)
    c: Coincident(g33,g28)
    c: Coincident(g33,g27)
    c: PointOnObject(g34,g27)
    c: Coincident(g34,g27)
    c: Equal(g34,g32)
    c: Coincident(g35,g34)
    c: PointOnObject(g35,g-32)
    c: Horizontal(g35)
    c: Coincident(g36,g-29)
    c: PointOnObject(g36,g29)
    c: Horizontal(g36)
    c: Coincident(g37,g36)
    c: Coincident(g37,g29)
    c: Coincident(g38,g29)
    c: Coincident(g38,g30)
    c: PointOnObject(g39,g-33)
    c: PointOnObject(g39,g30)
    c: Horizontal(g39)
    c: Coincident(g40,g39)
    c: Coincident(g40,g30)
    c: Equal(g37,g40)
    c: PointOnObject(g41,g-26)
    c: PointOnObject(g41,g-30)
    c: Vertical(g41)
    c: Coincident(g42,g41)
    c: Horizontal(g42)
    c: Coincident(g43,g42)
    c: PointOnObject(g43,g-35)
    c: Vertical(g43)
    c: Coincident(g44,g43)
    c: PointOnObject(g44,g-30)
    c: Horizontal(g44)
    c: Coincident(g45,g44)
    c: Coincident(g45,g-30)
    c: Equal(g31,g41)
    c: Equal(g43,g41)
    c: Coincident(g46,g42)
    c: PointOnObject(g46,g-36)
    c: Horizontal(g46)
    c: Coincident(g47,g43)
    c: PointOnObject(g47,g-36)
    c: Horizontal(g47)
    c: PointOnObject(g48,g-25)
    c: PointOnObject(g48,g-29)
    c: Vertical(g48)
    c: Coincident(g49,g48)
    c: Coincident(g49,g46)
    c: Horizontal(g49)
    c: Coincident(g50,g46)
    c: Coincident(g50,g47)
    c: Coincident(g51,g47)
    c: PointOnObject(g51,g-29)
    c: Horizontal(g51)
    c: Coincident(g52,g51)
    c: Coincident(g52,g-29)
    c: PointOnObject(g53,g-32)
    c: PointOnObject(g53,g-33)
    c: Horizontal(g53)
    c: PointOnObject(g54,g-32)
    c: PointOnObject(g54,g-33)
    c: Horizontal(g54)
    c: PointOnObject(g55,g-32)
    c: PointOnObject(g55,g-33)
    c: Horizontal(g55)
    c: PointOnObject(g56,g-32)
    c: PointOnObject(g56,g-33)
    c: Horizontal(g56)
    c: PointOnObject(g-3,g53)
    c: PointOnObject(g-4,g54)
    c: PointOnObject(g-5,g55)
    c: PointOnObject(g-6,g56)
    c: Coincident(g58,g8)
    c: Coincident(g58,g0)
    c: Coincident(g59,g57)
    c: Coincident(g59,g57)
    c: Vertical(g59)
    c: Coincident(g60,g57)
    c: PointOnObject(g60,g1)
    c: Horizontal(g60)
    c: Coincident(g61,g60)
    c: Coincident(g61,g1)
    c: Coincident(g57,g0)
    c: Coincident(g62,g1)
    c: Coincident(g62,g2)
    c: Coincident(g63,g2)
    c: PointOnObject(g63,g2)
    c: Coincident(g64,g63)
    c: PointOnObject(g64,g16)
    c: Horizontal(g64)
    c: Coincident(g65,g64)
    c: Coincident(g65,g16)
    c: Coincident(g66,g16)
    c: Coincident(g66,g21)
    c: PointOnObject(g64,g-37)
    c: PointOnObject(g60,g-37)
    c: Coincident(g67,g-18)
    c: PointOnObject(g67,g-21)
    c: Vertical(g67)
    c: Coincident(g68,g-17)
    c: PointOnObject(g68,g-21)
    c: Vertical(g68)
    c: Coincident(g69,g-16)
    c: PointOnObject(g69,g-21)
    c: Vertical(g69)
    c: Coincident(g70,g-15)
    c: PointOnObject(g70,g-21)
    c: Vertical(g70)
    c: Coincident(g71,g45)
    c: Coincident(g71,g67)
    c: Coincident(g72,g68)
    c: Coincident(g72,g69)
    c: Coincident(g73,g70)
    c: Coincident(g73,g52)
    c: Coincident(g75,g74)
    c: Coincident(g75,g74)
    c: Vertical(g75)
    c: Coincident(g74,g67)
    c: PointOnObject(g74,g-38)
    c: Coincident(g76,g74)
    c: PointOnObject(g76,g68)
    c: Horizontal(g76)
    c: Coincident(g77,g76)
    c: Coincident(g77,g68)
    c: Coincident(g78,g69)
    c: PointOnObject(g78,g-38)
    c: Vertical(g78)
    c: Coincident(g79,g78)
    c: PointOnObject(g79,g-38)
    c: Coincident(g80,g79)
    c: Coincident(g80,g70)
    c: Vertical(g80)
    c: Coincident(g81,g35)
    c: Coincident(g81,g56)
    c: Coincident(g82,g56)
    c: PointOnObject(g82,g-19)
    c: Horizontal(g82)
    c: Coincident(g83,g82)
    c: PointOnObject(g83,g-19)
    c: Coincident(g84,g83)
    c: Coincident(g84,g55)
    c: Horizontal(g84)
    c: Coincident(g85,g55)
    c: Coincident(g85,g54)
    c: Coincident(g86,g54)
    c: PointOnObject(g86,g-19)
    c: Horizontal(g86)
    c: Coincident(g87,g86)
    c: PointOnObject(g87,g-19)
    c: Coincident(g88,g87)
    c: Coincident(g88,g53)
    c: Horizontal(g88)
    c: Coincident(g89,g53)
    c: Coincident(g89,g13)
    c: Coincident(g90,g39)
    c: Coincident(g90,g56)
    c: Coincident(g91,g56)
    c: PointOnObject(g91,g56)
    c: Coincident(g92,g91)
    c: PointOnObject(g92,g-20)
    c: Vertical(g92)
    c: Coincident(g93,g92)
    c: Coincident(g93,g55)
    c: Coincident(g94,g55)
    c: Coincident(g94,g54)
    c: Horizontal(g93)
    c: Coincident(g95,g24)
    c: Coincident(g95,g53)
    c: Coincident(g96,g53)
    c: PointOnObject(g96,g-20)
    c: Horizontal(g96)
    c: Coincident(g97,g96)
    c: PointOnObject(g97,g-20)
    c: Coincident(g98,g97)
    c: Coincident(g98,g54)
FEATURE [Sketcher::SketchObject] Sketch006  label="CUT-ROOF"
  ArcFitTolerance = 0
  ExternalGeometry = -> [Sketch004,Sketch002,Sketch001]
  FullyConstrained = true
  MakeInternals = false
  MapMode = 2
  sketch-geometry (49):
    g0: LineSegment [constr] StartX=107.1 StartY=188.836 StartZ=0 EndX=107.1 EndY=44.8363 EndZ=0
    g1: LineSegment [constr] StartX=134.7 StartY=188.836 StartZ=0 EndX=134.7 EndY=44.8363 EndZ=0
    g2: LineSegment [constr] StartX=162.3 StartY=188.836 StartZ=0 EndX=162.3 EndY=44.8363 EndZ=0
    g3: LineSegment [constr] StartX=189.9 StartY=188.836 StartZ=0 EndX=189.9 EndY=44.8363 EndZ=0
    g4: LineSegment [constr] StartX=247.5 StartY=366.836 StartZ=0 EndX=395.5 EndY=218.836 EndZ=0
    g5: LineSegment [constr] StartX=395.5 StartY=218.836 StartZ=0 EndX=247.5 EndY=218.836 EndZ=0
    g6: LineSegment [constr] StartX=247.5 StartY=244.145 StartZ=0 EndX=370.192 EndY=244.145 EndZ=0
    g7: LineSegment [constr] StartX=247.5 StartY=274.818 StartZ=0 EndX=339.519 EndY=274.818 EndZ=0
    g8: LineSegment [constr] StartX=247.5 StartY=305.49 StartZ=0 EndX=308.846 EndY=305.49 EndZ=0
    g9: LineSegment [constr] StartX=247.5 StartY=336.163 StartZ=0 EndX=278.173 EndY=336.163 EndZ=0
    g10: LineSegment [constr] StartX=217.5 StartY=44.8363 StartZ=0 EndX=395.5 EndY=44.8363 EndZ=0
    g11: LineSegment [constr] StartX=395.5 StartY=44.8363 StartZ=0 EndX=395.5 EndY=218.836 EndZ=0
    g12: LineSegment [constr] StartX=395.5 StartY=44.8363 StartZ=0 EndX=247.5 EndY=192.836 EndZ=0
    g13: LineSegment [constr] StartX=278.173 StartY=336.163 StartZ=0 EndX=278.173 EndY=162.163 EndZ=0
    g14: LineSegment [constr] StartX=308.846 StartY=305.49 StartZ=0 EndX=308.846 EndY=131.49 EndZ=0
    g15: LineSegment [constr] StartX=339.519 StartY=274.818 StartZ=0 EndX=339.519 EndY=100.818 EndZ=0
    g16: LineSegment [constr] StartX=370.192 StartY=244.145 StartZ=0 EndX=370.192 EndY=70.1447 EndZ=0
    g17: LineSegment [constr] StartX=278.173 StartY=162.163 StartZ=0 EndX=79.5 EndY=162.163 EndZ=0
    g18: LineSegment [constr] StartX=308.846 StartY=131.49 StartZ=0 EndX=79.5 EndY=131.49 EndZ=0
    g19: LineSegment [constr] StartX=370.192 StartY=70.1447 StartZ=0 EndX=79.5 EndY=70.1447 EndZ=0
    g20: LineSegment StartX=213.5 StartY=188.836 StartZ=0 EndX=213.5 EndY=162.163 EndZ=0
    g21: LineSegment StartX=217.5 StartY=162.163 StartZ=0 EndX=213.5 EndY=162.163 EndZ=0
    g22: LineSegment StartX=217.5 StartY=162.163 StartZ=0 EndX=217.5 EndY=131.49 EndZ=0
    g23: LineSegment StartX=217.5 StartY=131.49 StartZ=0 EndX=213.5 EndY=131.49 EndZ=0
    g24: LineSegment [constr] StartX=339.519 StartY=100.818 StartZ=0 EndX=217.5 EndY=100.818 EndZ=0
    g25: LineSegment StartX=213.5 StartY=131.49 StartZ=0 EndX=213.5 EndY=100.818 EndZ=0
    g26: LineSegment StartX=213.5 StartY=100.818 StartZ=0 EndX=217.5 EndY=100.818 EndZ=0
    g27: LineSegment StartX=217.5 StartY=100.818 StartZ=0 EndX=217.5 EndY=70.1447 EndZ=0
    g28: LineSegment StartX=217.5 StartY=70.1447 StartZ=0 EndX=213.5 EndY=70.1447 EndZ=0
    g29: LineSegment StartX=213.5 StartY=70.1447 StartZ=0 EndX=213.5 EndY=48.8363 EndZ=0
    g30: LineSegment StartX=83.5 StartY=188.836 StartZ=0 EndX=83.5 EndY=162.163 EndZ=0
    g31: LineSegment StartX=83.5 StartY=162.163 StartZ=0 EndX=79.5 EndY=162.163 EndZ=0
    g32: LineSegment StartX=79.5 StartY=162.163 StartZ=0 EndX=79.5 EndY=131.49 EndZ=0
    g33: LineSegment StartX=79.5 StartY=131.49 StartZ=0 EndX=83.5 EndY=131.49 EndZ=0
    g34: LineSegment StartX=83.5 StartY=131.49 StartZ=0 EndX=83.5 EndY=100.818 EndZ=0
    g35: LineSegment StartX=83.5 StartY=100.818 StartZ=0 EndX=79.5 EndY=100.818 EndZ=0
    g36: LineSegment StartX=79.5 StartY=100.818 StartZ=0 EndX=79.5 EndY=70.1447 EndZ=0
    g37: LineSegment StartX=79.5 StartY=70.1447 StartZ=0 EndX=83.5 EndY=70.1447 EndZ=0
    g38: LineSegment StartX=83.5 StartY=70.1447 StartZ=0 EndX=83.5 EndY=48.8363 EndZ=0
    g39: LineSegment StartX=83.5 StartY=48.8363 StartZ=0 EndX=107.1 EndY=48.8363 EndZ=0
    g40: LineSegment StartX=107.1 StartY=48.8363 StartZ=0 EndX=107.1 EndY=44.8363 EndZ=0
    g41: LineSegment StartX=107.1 StartY=44.8363 StartZ=0 EndX=134.7 EndY=44.8363 EndZ=0
    g42: LineSegment StartX=162.3 StartY=44.8363 StartZ=0 EndX=189.9 EndY=44.8363 EndZ=0
    g43: LineSegment StartX=213.5 StartY=48.8363 StartZ=0 EndX=189.9 EndY=48.8363 EndZ=0
    g44: LineSegment StartX=189.9 StartY=48.8363 StartZ=0 EndX=189.9 EndY=44.8363 EndZ=0
    g45: LineSegment StartX=162.3 StartY=44.8363 StartZ=0 EndX=162.3 EndY=48.8363 EndZ=0
    g46: LineSegment StartX=162.3 StartY=48.8363 StartZ=0 EndX=134.7 EndY=48.8363 EndZ=0
    g47: LineSegment StartX=134.7 StartY=48.8363 StartZ=0 EndX=134.7 EndY=44.8363 EndZ=0
    g48: LineSegment [constr] StartX=217.5 StartY=100.818 StartZ=0 EndX=79.5 EndY=100.818 EndZ=0
  constraints (136):
    c: Coincident(g0,g-3)
    c: PointOnObject(g0,g-13)
    c: Vertical(g0)
    c: PointOnObject(g1,g-13)
    c: Vertical(g1)
    c: Coincident(g2,g-20)
    c: PointOnObject(g2,g-13)
    c: Vertical(g2)
    c: Coincident(g3,g-21)
    c: PointOnObject(g3,g-13)
    c: Vertical(g3)
    c: Coincident(g1,g-19)
    c: Coincident(g4,g-23)
    c: Coincident(g5,g4)
    c: Coincident(g5,g-23)
    c: Horizontal(g5)
    c: Angle(g4,g5) = 0.785398
    c: Coincident(g6,g-27)
    c: PointOnObject(g6,g4)
    c: Horizontal(g6)
    c: Coincident(g7,g-26)
    c: PointOnObject(g7,g4)
    c: Horizontal(g7)
    c: Coincident(g8,g-25)
    c: PointOnObject(g8,g4)
    c: Horizontal(g8)
    c: Coincident(g9,g-24)
    c: PointOnObject(g9,g4)
    c: Horizontal(g9)
    c: Coincident(g10,g-28)
    c: Horizontal(g10)
    c: Coincident(g11,g10)
    c: Coincident(g11,g4)
    c: Vertical(g11)
    c: Coincident(g12,g10)
    c: Angle(g12,g10) = 0.785398
    c: Horizontal(g12,g-21)
    c: Coincident(g13,g9)
    c: PointOnObject(g13,g12)
    c: Vertical(g13)
    c: Coincident(g14,g8)
    c: PointOnObject(g14,g12)
    c: Vertical(g14)
    c: Coincident(g15,g7)
    c: PointOnObject(g15,g12)
    c: Vertical(g15)
    c: Coincident(g16,g6)
    c: PointOnObject(g16,g12)
    c: Vertical(g16)
    c: Coincident(g17,g13)
    c: PointOnObject(g17,g-16)
    c: Horizontal(g17)
    c: Coincident(g18,g14)
    c: PointOnObject(g18,g-16)
    c: Horizontal(g18)
    c: Coincident(g19,g16)
    c: PointOnObject(g19,g-16)
    c: Horizontal(g19)
    c: Coincident(g20,g-17)
    c: PointOnObject(g20,g17)
    c: Vertical(g20)
    c: PointOnObject(g21,g17)
    c: Coincident(g21,g20)
    c: Coincident(g22,g21)
    c: PointOnObject(g22,g18)
    c: Vertical(g22)
    c: Coincident(g23,g22)
    c: PointOnObject(g23,g18)
    c: PointOnObject(g22,g-18)
    c: PointOnObject(g23,g-17)
    c: Coincident(g24,g15)
    c: PointOnObject(g24,g-18)
    c: Horizontal(g24)
    c: Coincident(g25,g23)
    c: PointOnObject(g25,g-17)
    c: Coincident(g26,g25)
    c: Coincident(g26,g24)
    c: Horizontal(g26)
    c: Coincident(g27,g24)
    c: PointOnObject(g27,g-18)
    c: Coincident(g28,g27)
    c: PointOnObject(g28,g-17)
    c: Horizontal(g28)
    c: Coincident(g29,g28)
    c: PointOnObject(g29,g-17)
    c: PointOnObject(g28,g19)
    c: PointOnObject(g29,g-14)
    c: Coincident(g30,g-15)
    c: PointOnObject(g30,g17)
    c: Vertical(g30)
    c: Coincident(g31,g30)
    c: Coincident(g31,g17)
    c: Coincident(g32,g17)
    c: Coincident(g32,g18)
    c: Coincident(g33,g18)
    c: PointOnObject(g33,g-15)
    c: Horizontal(g33)
    c: Coincident(g34,g33)
    c: PointOnObject(g34,g-15)
    c: Coincident(g35,g34)
    c: PointOnObject(g35,g-16)
    c: Horizontal(g35)
    c: Coincident(g36,g35)
    c: Coincident(g36,g19)
    c: Coincident(g37,g19)
    c: PointOnObject(g37,g19)
    c: Coincident(g38,g37)
    c: PointOnObject(g38,g-14)
    c: Vertical(g38)
    c: Coincident(g39,g38)
    c: PointOnObject(g39,g0)
    c: Horizontal(g39)
    c: Coincident(g40,g39)
    c: Coincident(g40,g0)
    c: Coincident(g41,g0)
    c: Coincident(g41,g1)
    c: Coincident(g42,g2)
    c: Coincident(g42,g3)
    c: Coincident(g43,g29)
    c: PointOnObject(g43,g3)
    c: Horizontal(g43)
    c: Coincident(g44,g43)
    c: Coincident(g44,g3)
    c: Coincident(g45,g2)
    c: PointOnObject(g45,g-14)
    c: Vertical(g45)
    c: Coincident(g46,g45)
    c: PointOnObject(g46,g1)
    c: Horizontal(g46)
    c: Coincident(g47,g46)
    c: Coincident(g47,g1)
    c: PointOnObject(g38,g-15)
    c: Coincident(g48,g24)
    c: PointOnObject(g48,g-16)
    c: Horizontal(g48)
    c: PointOnObject(g35,g48)
FEATURE [Part::Part2DObjectPython] Clone2D002  label="Model-CUT-BOX-WALLS"  # Draft 2D object (typed FeaturePython)
  Fuse = false
  Objects = -> [Sketch004]
  PathResource = Model
  Scale = (1,1,1)
FEATURE [Part::Part2DObjectPython] Clone2D003  label="Model-CUT-BOX-WALS2"  # Draft 2D object (typed FeaturePython)
  Fuse = false
  PathResource = Model
  Scale = (1,1,1)
FEATURE [Part::Part2DObjectPython] Clone2D004  label="Model-CUT-ROOF"  # Draft 2D object (typed FeaturePython)
  Fuse = false
  Objects = -> [Sketch006]
  PathResource = Model
  Scale = (1,1,1)
FEATURE [App::DocumentObjectGroup] Model
  Group = -> [Clone2D,Clone2D001,Clone2D002,Clone2D003,Clone2D004]
FEATURE [Path::FeaturePython] Job  # Path/CAM operation (typed FeaturePython)
  CycleTime = 00:00:04
  Fixtures = G54
  GeometryTolerance = 0.01
  JobType = 0
  Model = -> Model
  Operations = -> Operations
  OrderOutputBy = 0
  PostProcessor = 10
  PostProcessorOutputFile = <userpath>/Documents/AdruinoAtariPaddle/FREECAD/HousingAtari_RAW.nc
  SetupSheet = -> SetupSheet
  SplitOutput = false
  Stock = -> Stock001
  Tools = -> Tools
note: 1 file-system path scrubbed to <path> (originals preserved in the JSON sidecar)
